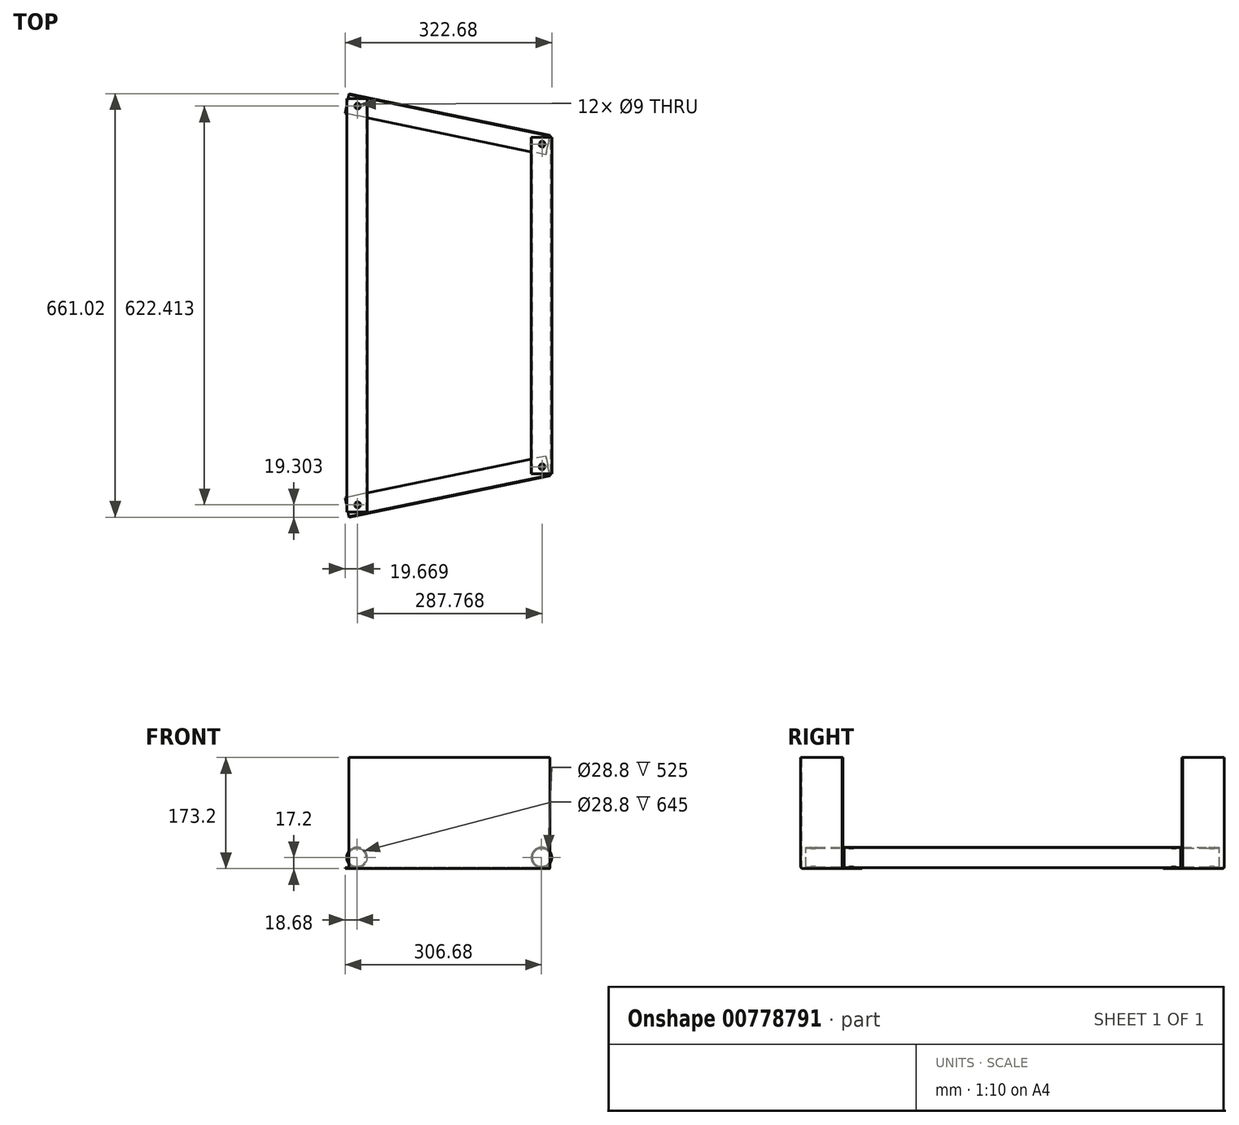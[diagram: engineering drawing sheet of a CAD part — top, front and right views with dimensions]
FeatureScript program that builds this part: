
annotation { "Feature Type Name" : "Feature", "Feature Type Description" : "" }
export const myFeature = defineFeature(function(context is Context, id is Id, definition is map)
    precondition{}
    {
        {
            var Q0;
            Q0=qCreatedBy(makeId("Front.planeOp"),FACE);
            var sketch = newSketch(context, id + "F0", { "sketchPlane" : qUnion([Q0])});
            skCircle(sketch, "E0", {"center": v(-144, 0) * mm, "radius": 16 * mm});
            skCircle(sketch, "E1.0", {"center": v(-144, 0) * mm, "radius": 14.4 * mm});
            skSolve(sketch);
        }
        {
            var Q0;
            Q0 = qSketchRegion(id + "F0", true);
            extrude(context, id + "F1", {"entities" : qUnion([Q0]), "depth" : 645 * mm, "offsetDistance" : 25 * mm, "symmetric" : true});
        }
        {
            var Q0;
            Q0=qCreatedBy(makeId("Front.planeOp"),FACE);
            var sketch = newSketch(context, id + "F2", { "sketchPlane" : qUnion([Q0])});
            skCircle(sketch, "E2", {"center": v(144, 0) * mm, "radius": 16 * mm});
            skCircle(sketch, "E3.0", {"center": v(144, 0) * mm, "radius": 14.4 * mm});
            skSolve(sketch);
        }
        {
            var Q0;
            Q0 = qSketchRegion(id + "F2", true);
            extrude(context, id + "F3", {"entities" : qUnion([Q0]), "depth" : 525 * mm, "offsetDistance" : 25 * mm, "symmetric" : true});
        }
        {
            var Q0;
            Q0=qCreatedBy(makeId("Top.planeOp"),FACE);
            var sketch = newSketch(context, id + "F4", { "sketchPlane" : qUnion([Q0])});
            skLineSegment(sketch, "E4", {"start": v(-156.6, -329.34) * mm, "end": v(156.76, -264.5) * mm});
            skLineSegment(sketch, "E5.0", {"start": v(-156.36, -330.51) * mm, "end": v(157, -265.68) * mm});
            skLineSegment(sketch, "E6", {"start": v(-156.6, -329.34) * mm, "end": v(-156.36, -330.51) * mm});
            skLineSegment(sketch, "E7", {"start": v(156.76, -264.5) * mm, "end": v(157, -265.68) * mm});
            skSolve(sketch);
        }
        {
            var Q0;
            Q0 = qSketchRegion(id + "F4", true);
            extrude(context, id + "F5", {"entities" : qUnion([Q0]), "depth" : 156 * mm, "offsetDistance" : 25 * mm});
        }
        {
            var Q0;
            Q0=makeQuery(id+"F5.opExtrude","SWEPT_FACE",FACE,{"disambiguationData":[OSD([sQuery(id+"F4.wireOp",EDGE,"E6")])]});
            var sketch = newSketch(context, id + "F6", { "sketchPlane" : qUnion([Q0])});
            skLineSegment(sketch, "E8", {"start": v(290.78, 0) * mm, "end": v(290.78, -14) * mm});
            skLineSegment(sketch, "E9", {"start": v(288.78, -16) * mm, "end": v(260.78, -16) * mm});
            skLineSegment(sketch, "E10", {"start": v(260.78, -16) * mm, "end": v(260.78, -17.2) * mm});
            skLineSegment(sketch, "E11", {"start": v(260.78, -17.2) * mm, "end": v(288.98, -17.2) * mm});
            skLineSegment(sketch, "E12", {"start": v(291.98, -14.2) * mm, "end": v(291.98, 0) * mm});
            skPoint(sketch, "E13.visualSharp", {"position": v(290.78, -16) * mm});
            skArc(sketch, "E13.filletArc", {"start": v(288.78, -16) * mm, "mid": v(290.19, -15.41) * mm, "end": v(290.78, -14) * mm});
            skPoint(sketch, "E14.visualSharp", {"position": v(291.98, -17.2) * mm});
            skArc(sketch, "E14.filletArc", {"start": v(288.98, -17.2) * mm, "mid": v(291.1, -16.32) * mm, "end": v(291.98, -14.2) * mm});
            skLineSegment(sketch, "E15", {"start": v(290.78, 0) * mm, "end": v(291.98, 0) * mm});
            skSolve(sketch);
        }
        {
            var Q0;
            Q0 = qSketchRegion(id + "F6", true);
            extrude(context, id + "F7", {"entities" : qUnion([Q0]), "operationType" : NewBodyOperationType.ADD, "oppositeDirection" : true, "depth" : 320 * mm, "offsetDistance" : 25 * mm});
        }
        {
            var Q0;
            Q0=makeQuery(id+"F5.opExtrude","SWEPT_BODY",BODY,{"disambiguationData":[OSD([sQuery(id+"F4.wireOp",EDGE,"E4"),sQuery(id+"F4.wireOp",EDGE,"E5.0"),sQuery(id+"F4.wireOp",EDGE,"E6"),sQuery(id+"F4.wireOp",EDGE,"E7")])]});
            var Q1;
            Q1=qCreatedBy(makeId("Front.planeOp"),FACE);
            mirror(context, id + "F8", {"entities" : qUnion([Q0]), "mirrorPlane" : qUnion([Q1])});
        }
        {
            var Q0;
            Q0=qCreatedBy(makeId("Top.planeOp"),FACE);
            var sketch = newSketch(context, id + "F9", { "sketchPlane" : qUnion([Q0])});
            skCircle(sketch, "E16", {"center": v(-143.01, -311.2) * mm, "radius": 4.5 * mm});
            skCircle(sketch, "E17", {"center": v(144.76, -251.67) * mm, "radius": 4.5 * mm});
            skCircle(sketch, "E18", {"center": v(144.76, 251.67) * mm, "radius": 4.5 * mm});
            skCircle(sketch, "E19", {"center": v(-143.01, 311.2) * mm, "radius": 4.5 * mm});
            skSolve(sketch);
        }
        {
            var Q0;
            Q0 = qSketchRegion(id + "F9", true);
            extrude(context, id + "F10", {"entities" : qUnion([Q0]), "operationType" : NewBodyOperationType.REMOVE, "oppositeDirection" : true, "depth" : 36 * mm, "offsetDistance" : 25 * mm, "symmetric" : true});
        }
    });
